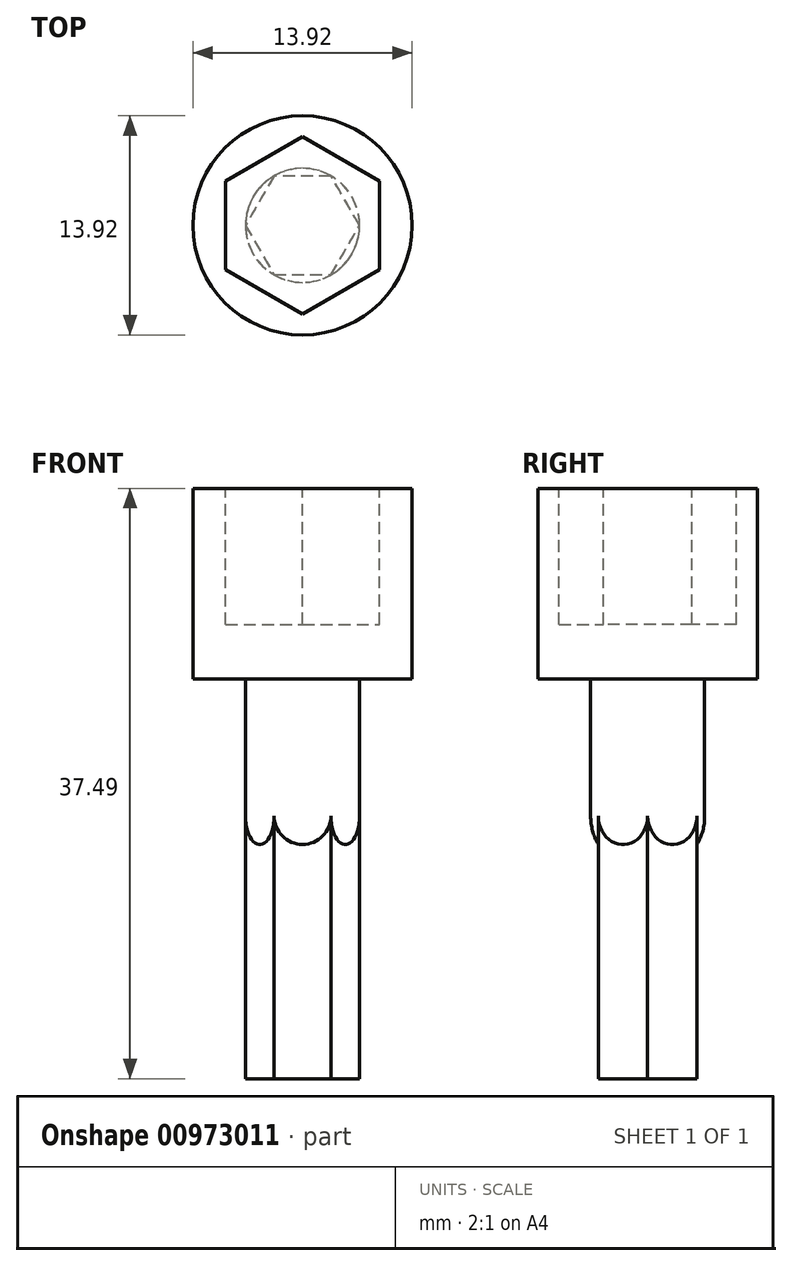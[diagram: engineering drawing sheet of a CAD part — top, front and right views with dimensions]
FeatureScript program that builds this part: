
annotation { "Feature Type Name" : "Feature", "Feature Type Description" : "" }
export const myFeature = defineFeature(function(context is Context, id is Id, definition is map)
    precondition{}
    {
        {
            var Q0;
            Q0=qCreatedBy(makeId("Top.planeOp"),FACE);
            var sketch = newSketch(context, id + "F0", { "sketchPlane" : qUnion([Q0])});
            skCircle(sketch, "E0", {"center": v(0, 0) * mm, "radius": 6.96 * mm});
            skSolve(sketch);
        }
        {
            var Q0;
            Q0 = qSketchRegion(id + "F0", true);
            extrude(context, id + "F1", {"entities" : qUnion([Q0]), "depth" : 12.1 * mm, "offsetDistance" : 25.4 * mm});
        }
        {
            var Q0;
            Q0=makeQuery(id+"F1.opExtrude","CAP_FACE",FACE,{"disambiguationData":[OSD([sQuery(id+"F0.wireOp",EDGE,"E0")])],"isStart":false});
            var sketch = newSketch(context, id + "F2", { "sketchPlane" : qUnion([Q0])});
            skCircle(sketch, "E1.cCircle", {"center": v(0, 0) * mm, "radius": 4.88 * mm, "construction": true});
            skLineSegment(sketch, "E1.0", {"start": v(4.88, 2.82) * mm, "end": v(4.88, -2.82) * mm});
            skLineSegment(sketch, "E1.1", {"start": v(4.88, -2.82) * mm, "end": v(0, -5.63) * mm});
            skLineSegment(sketch, "E1.2", {"start": v(0, -5.63) * mm, "end": v(-4.88, -2.82) * mm});
            skLineSegment(sketch, "E1.3", {"start": v(-4.88, -2.82) * mm, "end": v(-4.88, 2.82) * mm});
            skLineSegment(sketch, "E1.4", {"start": v(-4.88, 2.82) * mm, "end": v(0, 5.63) * mm});
            skLineSegment(sketch, "E1.5", {"start": v(0, 5.63) * mm, "end": v(4.88, 2.82) * mm});
            skPoint(sketch, "E1.0.midPoint", {"position": v(4.88, 0) * mm});
            skSolve(sketch);
        }
        {
            var Q0;
            Q0 = qSketchRegion(id + "F2", true);
            var Q1;
            Q1=makeQuery(id+"F2.imprint","IMPRINT",FACE,{"disambiguationData":[TD([[makeQuery(id+"F2.imprint","IMPRINT",EDGE,{"derivedFrom":sQuery(id+"F2.wireOp",EDGE,"E1.0")}),-1.0]])]});
            extrude(context, id + "F3", {"entities" : qUnion([Q0, Q1]), "operationType" : NewBodyOperationType.REMOVE, "oppositeDirection" : true, "depth" : 8.64 * mm, "offsetDistance" : 25.4 * mm});
        }
        {
            var Q0;
            Q0=makeQuery(id+"F1.opExtrude","CAP_FACE",FACE,{"disambiguationData":[OSD([sQuery(id+"F0.wireOp",EDGE,"E0")])],"isStart":true});
            var sketch = newSketch(context, id + "F4", { "sketchPlane" : qUnion([Q0])});
            skCircle(sketch, "E2.cCircle", {"center": v(0, 0) * mm, "radius": 3.14 * mm, "construction": true});
            skLineSegment(sketch, "E2.0", {"start": v(1.81, -3.14) * mm, "end": v(-1.81, -3.14) * mm});
            skLineSegment(sketch, "E2.1", {"start": v(-1.81, -3.14) * mm, "end": v(-3.62, 0) * mm});
            skLineSegment(sketch, "E2.2", {"start": v(-3.62, 0) * mm, "end": v(-1.81, 3.14) * mm});
            skLineSegment(sketch, "E2.3", {"start": v(-1.81, 3.14) * mm, "end": v(1.81, 3.14) * mm});
            skLineSegment(sketch, "E2.4", {"start": v(1.81, 3.14) * mm, "end": v(3.62, 0) * mm});
            skLineSegment(sketch, "E2.5", {"start": v(3.62, 0) * mm, "end": v(1.81, -3.14) * mm});
            skPoint(sketch, "E2.0.midPoint", {"position": v(0, -3.14) * mm});
            skSolve(sketch);
        }
        {
            var Q0;
            Q0=makeQuery(id+"F4.imprint","IMPRINT",FACE,{"disambiguationData":[TD([[makeQuery(id+"F4.imprint","IMPRINT",EDGE,{"derivedFrom":sQuery(id+"F4.wireOp",EDGE,"E2.0")}),-1.0]])]});
            extrude(context, id + "F5", {"entities" : qUnion([Q0]), "operationType" : NewBodyOperationType.ADD, "depth" : 25.4 * mm, "offsetDistance" : 25.4 * mm});
        }
        {
            var Q0;
            Q0=qCreatedBy(makeId("Front.planeOp"),FACE);
            var sketch = newSketch(context, id + "F6", { "sketchPlane" : qUnion([Q0])});
            skPoint(sketch, "E3.0", {"position": v(-3.62, 0) * mm});
            skPoint(sketch, "E3.1", {"position": v(3.62, 0) * mm});
            skLineSegment(sketch, "E4.bottom", {"start": v(-3.62, 0) * mm, "end": v(0, 0) * mm});
            skLineSegment(sketch, "E4.left", {"start": v(-3.62, 0) * mm, "end": v(-3.62, -8.71) * mm});
            skArc(sketch, "E5", {"start": v(-3.62, -8.71) * mm, "mid": v(-2.56, -11.27) * mm, "end": v(0, -12.33) * mm});
            skLineSegment(sketch, "E6", {"start": v(0, 0) * mm, "end": v(0, -12.33) * mm});
            skPoint(sketch, "E7.orphan", {"position": v(3.62, -8.71) * mm});
            skSolve(sketch);
        }
        {
            var Q0;
            Q0 = qSketchRegion(id + "F6", true);
            var Q1;
            Q1=sQuery(id+"F6.wireOp",EDGE,"E6");
            revolve(context, id + "F7", {"operationType" : NewBodyOperationType.ADD, "surfaceOperationType" : NewSurfaceOperationType.NEW, "entities" : qUnion([Q0]), "axis" : qUnion([Q1]), "revolveType" : RevolveType.FULL});
        }
    });
